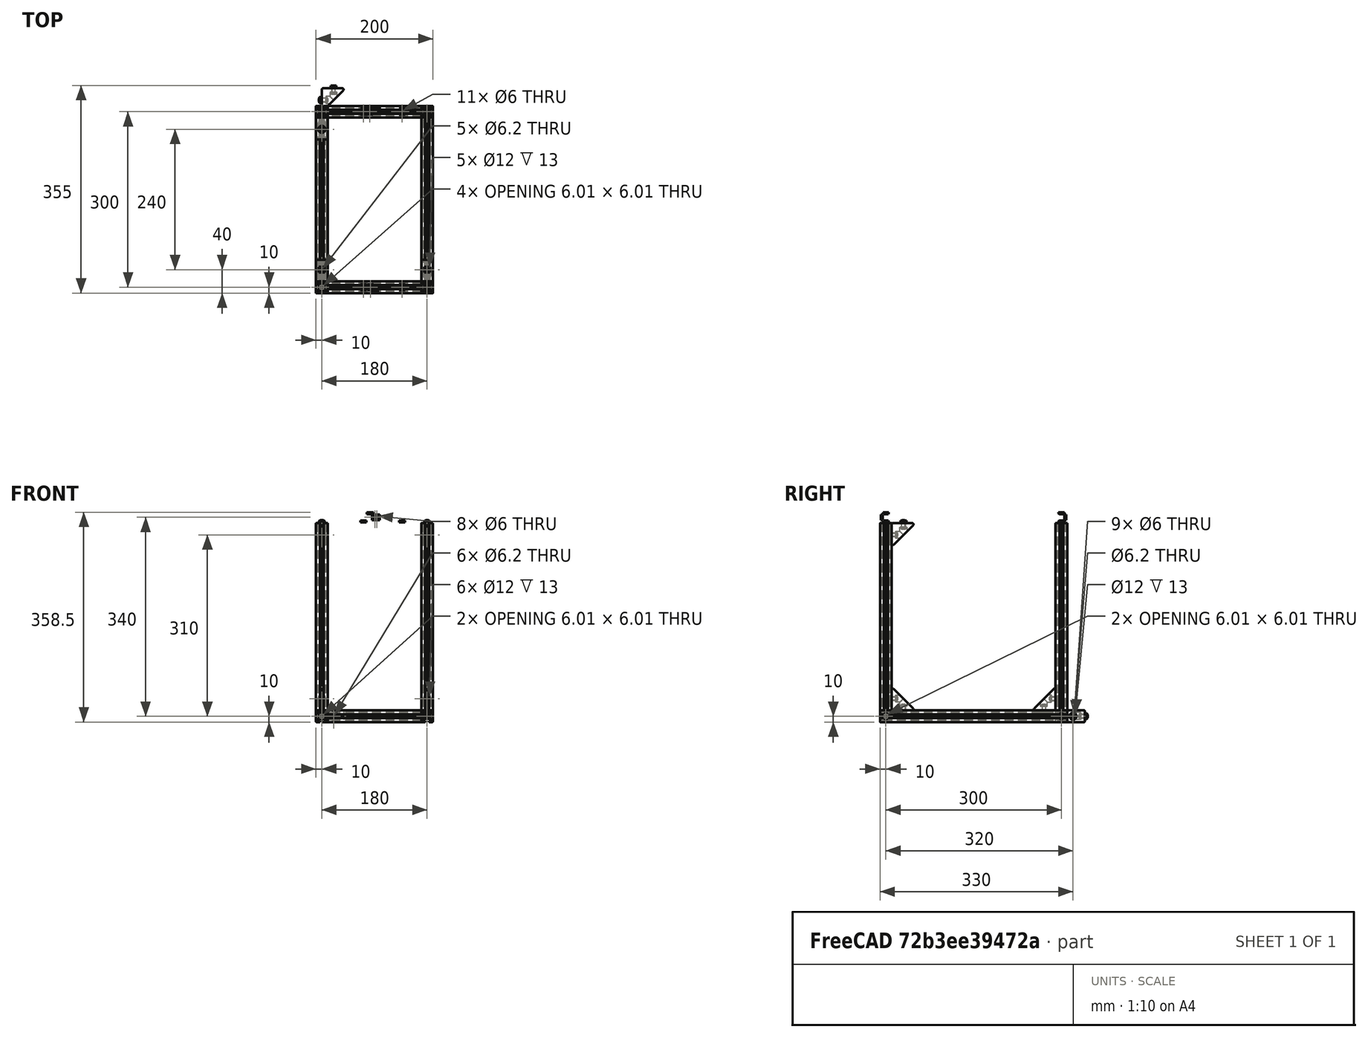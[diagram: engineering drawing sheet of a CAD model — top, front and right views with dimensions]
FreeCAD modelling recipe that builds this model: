
FCSTD DOCUMENT  (FreeCAD 0.17R9796 (Git))
Label: upright1
License: All rights reserved
LicenseURL: http://en.wikipedia.org/wiki/All_rights_reserved
objects: Part::Feature×57, Part::FeaturePython×16, App::Part×6, Part::Compound×5
note: 78 computed .brp shape members not serialized (recipe doc carries the construction recipe); baked Part::Feature solids carry a one-line shape summary decoded from their .brp

FEATURE [Part::Feature] Pocket003001  label="tslot32con"
  Placement = pos=(0,10,10) rot=(1,0,0;1.5708rad)
  shape: bbox 20 x 320 x 20 mm, 150 faces (baked)
FEATURE [Part::Feature] Pocket003002  label="tslot16"
  Placement = pos=(10,0,10) rot=(0,1,0;1.5708rad)
  shape: bbox 160 x 20 x 20 mm, 94 faces (baked)
FEATURE [Part::Feature] Pocket003006  label="tslot16_001"
  Placement = pos=(10,-300,10) rot=(0,1,0;1.5708rad)
  shape: bbox 160 x 20 x 20 mm, 94 faces (baked)
FEATURE [Part::Feature] Pocket003007  label="tslot32con_001"
  Placement = pos=(180,-310,10) rot=(0,0.707107,0.707107;3.14159rad)
  shape: bbox 20 x 320 x 20 mm, 150 faces (baked)
FEATURE [Part::FeaturePython] Screw  label="M6x25-Screw"  # Fasteners workbench fastener (typed FeaturePython)
  Placement = pos=(-4,0,10) rot=(0,-1,0;1.5708rad)
  diameter = 7
  invert = false
  length = 6
  matchOuter = false
  offset = 0
  thread = false
  type = 15
FEATURE [Part::FeaturePython] Screw001  label="M6x25-Screw004"  # Fasteners workbench fastener (typed FeaturePython)
  Placement = pos=(-4,-300,10) rot=(0,-1,0;1.5708rad)
  diameter = 7
  invert = false
  length = 6
  matchOuter = false
  offset = 0
  thread = false
  type = 15
FEATURE [Part::FeaturePython] Screw002  label="M6x25-Screw005"  # Fasteners workbench fastener (typed FeaturePython)
  Placement = pos=(184,0,10) rot=(0,1,0;1.5708rad)
  diameter = 7
  invert = false
  length = 6
  matchOuter = false
  offset = 0
  thread = false
  type = 15
FEATURE [Part::FeaturePython] Screw004  label="M6x25-Screw006"  # Fasteners workbench fastener (typed FeaturePython)
  Placement = pos=(184,-300,10) rot=(0,1,0;1.5708rad)
  diameter = 7
  invert = false
  length = 6
  matchOuter = false
  offset = 0
  thread = false
  type = 15
FEATURE [App::Part] Part  label="lower_frame"
  Group = -> [Pocket003001,Pocket003002,Pocket003006,Pocket003007,Screw,Screw001,Screw002,Screw004]
  License = CC BY 3.0
  LicenseURL = http://creativecommons.org/licenses/by/3.0/
  Origin = -> PartOrigin
FEATURE [Part::Feature] Pocket003008  label="tslot32con001"
  Placement = pos=(0,10,10) rot=(1,0,0;1.5708rad)
  shape: bbox 20 x 320 x 20 mm, 150 faces (baked)
FEATURE [Part::Feature] Pocket003009  label="tslot041"
  Placement = pos=(10,0,10) rot=(0,1,0;1.5708rad)
  shape: bbox 160 x 20 x 20 mm, 94 faces (baked)
FEATURE [Part::Feature] Pocket003010  label="tslot16_002"
  Placement = pos=(10,-300,10) rot=(0,1,0;1.5708rad)
  shape: bbox 160 x 20 x 20 mm, 94 faces (baked)
FEATURE [Part::Feature] Pocket003011  label="tslot32con_002"
  Placement = pos=(180,-310,10) rot=(0,0.707107,0.707107;3.14159rad)
  shape: bbox 20 x 320 x 20 mm, 150 faces (baked)
FEATURE [Part::FeaturePython] Screw005  label="M6x25-Screw007"  # Fasteners workbench fastener (typed FeaturePython)
  Placement = pos=(-4,0,10) rot=(0,-1,0;1.5708rad)
  diameter = 7
  invert = false
  length = 6
  matchOuter = false
  offset = 0
  thread = false
  type = 15
FEATURE [Part::FeaturePython] Screw006  label="M6x25-Screw008"  # Fasteners workbench fastener (typed FeaturePython)
  Placement = pos=(-4,-300,10) rot=(0,-1,0;1.5708rad)
  diameter = 7
  invert = false
  length = 6
  matchOuter = false
  offset = 0
  thread = false
  type = 15
FEATURE [Part::FeaturePython] Screw007  label="M6x25-Screw011"  # Fasteners workbench fastener (typed FeaturePython)
  Placement = pos=(184,0,10) rot=(0,1,0;1.5708rad)
  diameter = 7
  invert = false
  length = 6
  matchOuter = false
  offset = 0
  thread = false
  type = 15
FEATURE [Part::FeaturePython] Screw008  label="M6x25-Screw010"  # Fasteners workbench fastener (typed FeaturePython)
  Placement = pos=(184,-300,10) rot=(0,1,0;1.5708rad)
  diameter = 7
  invert = false
  length = 6
  matchOuter = false
  offset = 0
  thread = false
  type = 15
FEATURE [App::Part] Part001  label="upper_frame"
  Group = -> [Pocket003008,Pocket003009,Pocket003010,Pocket003011,Screw005,Screw006,Screw007,Screw008]
  License = CC BY 3.0
  LicenseURL = http://creativecommons.org/licenses/by/3.0/
  Origin = -> PartOrigin001
  Placement = pos=(0,0,340) rot=(0,0,1;0rad)
FEATURE [Part::Feature] Fillet004001  label="Fillet005"
  shape: bbox 37.5 x 37.5 x 20 mm, 26 faces (baked)
FEATURE [Part::FeaturePython] Screw009  label="M6x12-Screw"  # Fasteners workbench fastener (typed FeaturePython)
  Placement = pos=(7,20,10) rot=(0,1,0;1.5708rad)
  diameter = 4
  invert = false
  length = 1
  matchOuter = false
  offset = 0
  thread = false
  type = 20
FEATURE [Part::Feature] Body001  label="m6nutplate"
  Placement = pos=(-1.5,15,5) rot=(0,-1,0;1.5708rad)
  shape: bbox 3 x 10 x 10 mm, 9 faces (baked)
FEATURE [App::Part] Part002  label="cornerstonescrewnut"
  License = CC BY 3.0
  LicenseURL = http://creativecommons.org/licenses/by/3.0/
  Origin = -> PartOrigin002
  Placement = pos=(10,-50,20) rot=(0,-1,0;1.5708rad)
FEATURE [Part::FeaturePython] Screw010  label="M6x12-Screw001"  # Fasteners workbench fastener (typed FeaturePython)
  Placement = pos=(20,33,10) rot=(1,0,0;1.5708rad)
  diameter = 4
  invert = false
  length = 1
  matchOuter = false
  offset = 0
  thread = false
  type = 20
FEATURE [Part::Feature] Body002  label="m6nutplate001"
  Placement = pos=(15,41.5,5) rot=(0.57735,0.57735,0.57735;4.18879rad)
  shape: bbox 10 x 3 x 10 mm, 9 faces (baked)
FEATURE [Part::Feature] Fillet004002  label="Fillet006"
  shape: bbox 37.5 x 37.5 x 20 mm, 26 faces (baked)
FEATURE [Part::FeaturePython] Screw011  label="M6x12-Screw002"  # Fasteners workbench fastener (typed FeaturePython)
  Placement = pos=(7,20,10) rot=(0,1,0;1.5708rad)
  diameter = 4
  invert = false
  length = 1
  matchOuter = false
  offset = 0
  thread = false
  type = 20
FEATURE [Part::Feature] Body003  label="m6nutplate002"
  Placement = pos=(-1.5,15,5) rot=(0,-1,0;1.5708rad)
  shape: bbox 3 x 10 x 10 mm, 9 faces (baked)
FEATURE [Part::FeaturePython] Screw012  label="M6x12-Screw003"  # Fasteners workbench fastener (typed FeaturePython)
  Placement = pos=(20,33,10) rot=(1,0,0;1.5708rad)
  diameter = 4
  invert = false
  length = 1
  matchOuter = false
  offset = 0
  thread = false
  type = 20
FEATURE [Part::Feature] Body004  label="m6nutplate003"
  Placement = pos=(15,41.5,5) rot=(0.57735,0.57735,0.57735;4.18879rad)
  shape: bbox 10 x 3 x 10 mm, 9 faces (baked)
FEATURE [App::Part] Part003  label="cornerstonescrewnut001"
  Group = -> [Body003,Screw011,Fillet004002,Screw012,Body004,PartOrigin002,Body001,Screw009,Fillet004001,Screw010,Body002,Part002]
  License = CC BY 3.0
  LicenseURL = http://creativecommons.org/licenses/by/3.0/
  Origin = -> PartOrigin003
  Placement = pos=(190,-50,20) rot=(0,-1,0;1.5708rad)
FEATURE [Part::Feature] Fillet004003  label="Fillet007"
  shape: bbox 37.5 x 37.5 x 20 mm, 26 faces (baked)
FEATURE [Part::FeaturePython] Screw013  label="M6x12-Screw004"  # Fasteners workbench fastener (typed FeaturePython)
  Placement = pos=(7,20,10) rot=(0,1,0;1.5708rad)
  diameter = 4
  invert = false
  length = 1
  matchOuter = false
  offset = 0
  thread = false
  type = 20
FEATURE [Part::Feature] Body005  label="m6nutplate004"
  Placement = pos=(-1.5,15,5) rot=(0,-1,0;1.5708rad)
  shape: bbox 3 x 10 x 10 mm, 9 faces (baked)
FEATURE [Part::FeaturePython] Screw014  label="M6x12-Screw005"  # Fasteners workbench fastener (typed FeaturePython)
  Placement = pos=(20,33,10) rot=(1,0,0;1.5708rad)
  diameter = 4
  invert = false
  length = 1
  matchOuter = false
  offset = 0
  thread = false
  type = 20
FEATURE [Part::Feature] Body006  label="m6nutplate005"
  Placement = pos=(15,41.5,5) rot=(0.57735,0.57735,0.57735;4.18879rad)
  shape: bbox 10 x 3 x 10 mm, 9 faces (baked)
FEATURE [App::Part] Part004  label="cornerstonescrewnut002"
  Group = -> [Body005,Screw013,Fillet004003,Screw014,Body006]
  License = CC BY 3.0
  LicenseURL = http://creativecommons.org/licenses/by/3.0/
  Origin = -> PartOrigin004
  Placement = pos=(-10,-50,340) rot=(0,1,0;1.5708rad)
FEATURE [Part::Feature] Fillet004004  label="Fillet008"
  shape: bbox 37.5 x 37.5 x 20 mm, 26 faces (baked)
FEATURE [Part::FeaturePython] Screw015  label="M6x12-Screw006"  # Fasteners workbench fastener (typed FeaturePython)
  Placement = pos=(7,20,10) rot=(0,1,0;1.5708rad)
  diameter = 4
  invert = false
  length = 1
  matchOuter = false
  offset = 0
  thread = false
  type = 20
FEATURE [Part::Feature] Body007  label="m6nutplate006"
  Placement = pos=(-1.5,15,5) rot=(0,-1,0;1.5708rad)
  shape: bbox 3 x 10 x 10 mm, 9 faces (baked)
FEATURE [Part::FeaturePython] Screw016  label="M6x12-Screw007"  # Fasteners workbench fastener (typed FeaturePython)
  Placement = pos=(20,33,10) rot=(1,0,0;1.5708rad)
  diameter = 4
  invert = false
  length = 1
  matchOuter = false
  offset = 0
  thread = false
  type = 20
FEATURE [Part::Feature] Body008  label="m6nutplate007"
  Placement = pos=(15,41.5,5) rot=(0.57735,0.57735,0.57735;4.18879rad)
  shape: bbox 10 x 3 x 10 mm, 9 faces (baked)
FEATURE [App::Part] Part005  label="cornerstonescrewnut003"
  Group = -> [Body007,Screw015,Fillet004004,Screw016,Body008]
  License = CC BY 3.0
  LicenseURL = http://creativecommons.org/licenses/by/3.0/
  Origin = -> PartOrigin005
  Placement = pos=(170,-50,340) rot=(0,1,0;1.5708rad)
FEATURE [Part::Feature] Body009001  label="m6nutplate010"
  Placement = pos=(-1.5,15,5) rot=(0,-1,0;1.5708rad)
  shape: bbox 3 x 10 x 10 mm, 9 faces (baked)
FEATURE [Part::Feature] Body010001  label="m6nutplate011"
  Placement = pos=(15,41.5,5) rot=(0.57735,0.57735,0.57735;4.18879rad)
  shape: bbox 10 x 3 x 10 mm, 9 faces (baked)
FEATURE [Part::Feature] Screw018001  label="M6x12-Screw010"
  Placement = pos=(20,33,10) rot=(1,0,0;1.5708rad)
  shape: bbox 10.5 x 15.3 x 10.5 mm, 15 faces (baked)
FEATURE [Part::Feature] Screw017001  label="M6x12-Screw011"
  Placement = pos=(7,20,10) rot=(0,1,0;1.5708rad)
  shape: bbox 15.3 x 10.5 x 10.5 mm, 15 faces (baked)
FEATURE [Part::Feature] Fillet004005001  label="Fillet010"
  shape: bbox 37.5 x 37.5 x 20 mm, 26 faces (baked)
FEATURE [Part::Compound] Compound
  Links = -> [Body009001,Fillet004005001,Screw017001,Body010001,Screw018001]
  Placement = pos=(10,-250,340) rot=(0.707107,0,-0.707107;3.14159rad)
FEATURE [Part::Feature] Body010002  label="m6nutplate012"
  Placement = pos=(-1.5,15,5) rot=(0,-1,0;1.5708rad)
  shape: bbox 3 x 10 x 10 mm, 9 faces (baked)
FEATURE [Part::Feature] Body010003  label="m6nutplate013"
  Placement = pos=(15,41.5,5) rot=(0.57735,0.57735,0.57735;4.18879rad)
  shape: bbox 10 x 3 x 10 mm, 9 faces (baked)
FEATURE [Part::Feature] Screw018002  label="M6x12-Screw012"
  Placement = pos=(20,33,10) rot=(1,0,0;1.5708rad)
  shape: bbox 10.5 x 15.3 x 10.5 mm, 15 faces (baked)
FEATURE [Part::Feature] Screw018003  label="M6x12-Screw013"
  Placement = pos=(7,20,10) rot=(0,1,0;1.5708rad)
  shape: bbox 15.3 x 10.5 x 10.5 mm, 15 faces (baked)
FEATURE [Part::Feature] Fillet004005002  label="Fillet011"
  shape: bbox 37.5 x 37.5 x 20 mm, 26 faces (baked)
FEATURE [Part::Compound] Compound001
  Links = -> [Body010002,Fillet004005002,Screw018003,Body010003,Screw018002]
  Placement = pos=(190,-250,340) rot=(0.707107,0,-0.707107;3.14159rad)
FEATURE [Part::Feature] Body010004  label="m6nutplate014"
  Placement = pos=(-1.5,15,5) rot=(0,-1,0;1.5708rad)
  shape: bbox 3 x 10 x 10 mm, 9 faces (baked)
FEATURE [Part::Feature] Body010005  label="m6nutplate015"
  Placement = pos=(15,41.5,5) rot=(0.57735,0.57735,0.57735;4.18879rad)
  shape: bbox 10 x 3 x 10 mm, 9 faces (baked)
FEATURE [Part::Feature] Screw018004  label="M6x12-Screw014"
  Placement = pos=(20,33,10) rot=(1,0,0;1.5708rad)
  shape: bbox 10.5 x 15.3 x 10.5 mm, 15 faces (baked)
FEATURE [Part::Feature] Screw018005  label="M6x12-Screw015"
  Placement = pos=(7,20,10) rot=(0,1,0;1.5708rad)
  shape: bbox 15.3 x 10.5 x 10.5 mm, 15 faces (baked)
FEATURE [Part::Feature] Fillet004005003  label="Fillet012"
  shape: bbox 37.5 x 37.5 x 20 mm, 26 faces (baked)
FEATURE [Part::Compound] Compound002
  Links = -> [Body010004,Fillet004005003,Screw018005,Body010005,Screw018004]
  Placement = pos=(10,-290,60) rot=(0.57735,0.57735,-0.57735;4.18879rad)
FEATURE [Part::Feature] Body010006  label="m6nutplate016"
  Placement = pos=(-1.5,15,5) rot=(0,-1,0;1.5708rad)
  shape: bbox 3 x 10 x 10 mm, 9 faces (baked)
FEATURE [Part::Feature] Body010007  label="m6nutplate017"
  Placement = pos=(15,41.5,5) rot=(0.57735,0.57735,0.57735;4.18879rad)
  shape: bbox 10 x 3 x 10 mm, 9 faces (baked)
FEATURE [Part::Feature] Screw018006  label="M6x12-Screw016"
  Placement = pos=(20,33,10) rot=(1,0,0;1.5708rad)
  shape: bbox 10.5 x 15.3 x 10.5 mm, 15 faces (baked)
FEATURE [Part::Feature] Screw018007  label="M6x12-Screw017"
  Placement = pos=(7,20,10) rot=(0,1,0;1.5708rad)
  shape: bbox 15.3 x 10.5 x 10.5 mm, 15 faces (baked)
FEATURE [Part::Feature] Fillet004005004  label="Fillet013"
  shape: bbox 37.5 x 37.5 x 20 mm, 26 faces (baked)
FEATURE [Part::Compound] Compound003
  Links = -> [Body010006,Fillet004005004,Screw018007,Body010007,Screw018006]
  Placement = pos=(190,-290,60) rot=(0.57735,0.57735,-0.57735;4.18879rad)
FEATURE [Part::Feature] Pocket001001  label="tslot32"
  Placement = pos=(0,0,20) rot=(0,0,1;0rad)
  shape: bbox 20 x 20 x 320 mm, 94 faces (baked)
FEATURE [Part::Feature] Body010008  label="m6nutplate018"
  Placement = pos=(-1.5,15,5) rot=(0,-1,0;1.5708rad)
  shape: bbox 3 x 10 x 10 mm, 9 faces (baked)
FEATURE [Part::Feature] Body010009  label="m6nutplate019"
  Placement = pos=(15,41.5,5) rot=(0.57735,0.57735,0.57735;4.18879rad)
  shape: bbox 10 x 3 x 10 mm, 9 faces (baked)
FEATURE [Part::Feature] Screw018008  label="M6x12-Screw018"
  Placement = pos=(20,33,10) rot=(1,0,0;1.5708rad)
  shape: bbox 10.5 x 15.3 x 10.5 mm, 15 faces (baked)
FEATURE [Part::Feature] Screw018009  label="M6x12-Screw019"
  Placement = pos=(7,20,10) rot=(0,1,0;1.5708rad)
  shape: bbox 15.3 x 10.5 x 10.5 mm, 15 faces (baked)
FEATURE [Part::Feature] Fillet004005005  label="Fillet014"
  shape: bbox 37.5 x 37.5 x 20 mm, 26 faces (baked)
FEATURE [Part::Compound] Compound004
  Links = -> [Body010008,Fillet004005005,Screw018009,Body010009,Screw018008]
  Placement = pos=(-10,-10,60) rot=(0.57735,-0.57735,0.57735;4.18879rad)
FEATURE [Part::Feature] Pocket003012  label="tslot32_001"
  Placement = pos=(0,-300,20) rot=(0,0,1;0rad)
  shape: bbox 20 x 20 x 320 mm, 94 faces (baked)
FEATURE [Part::Feature] Pocket003013  label="tslot32_002"
  Placement = pos=(180,0,20) rot=(0,0,1;0rad)
  shape: bbox 20 x 20 x 320 mm, 94 faces (baked)
FEATURE [Part::Feature] Pocket003014  label="tslot32_003"
  Placement = pos=(180,-300,20) rot=(0,0,1;0rad)
  shape: bbox 20 x 20 x 320 mm, 94 faces (baked)
FEATURE [Part::Feature] Chamfer001001  label="m6nutplate020"
  Placement = pos=(88,-295,358.5) rot=(-0.707107,0.707107,0;3.14159rad)
  shape: bbox 10 x 10 x 3 mm, 9 faces (baked)
FEATURE [Part::Feature] Chamfer001002  label="m6nutplate021"
  Placement = pos=(96,-308.5,355) rot=(0.57735,-0.57735,-0.57735;4.18879rad)
  shape: bbox 10 x 3 x 10 mm, 9 faces (baked)
FEATURE [Part::Feature] Chamfer001003  label="m6nutplate022"
  Placement = pos=(87,5,358.5) rot=(0.707107,-0.707107,0;3.14159rad)
  shape: bbox 10 x 10 x 3 mm, 9 faces (baked)
FEATURE [Part::Feature] Chamfer001004  label="m6nutplate023"
  Placement = pos=(99,8.4,345) rot=(0.57735,-0.57735,0.57735;2.0944rad)
  shape: bbox 10 x 3 x 10 mm, 9 faces (baked)
FEATURE [Part::Feature] Chamfer001005  label="m6nutplate024"
  Placement = pos=(76,-305,341.6) rot=(0,0,1;1.5708rad)
  shape: bbox 10 x 10 x 3 mm, 9 faces (baked)
FEATURE [Part::Feature] Chamfer001006  label="m6nutplate025"
  Placement = pos=(142,-305,341.6) rot=(0,0,1;1.5708rad)
  shape: bbox 10 x 10 x 3 mm, 9 faces (baked)
FEATURE [Part::Feature] Chamfer001007  label="m6nutplate026"
  Placement = pos=(142,-5,341.6) rot=(0,0,1;1.5708rad)
  shape: bbox 10 x 10 x 3 mm, 9 faces (baked)
FEATURE [Part::Feature] Chamfer001008  label="m6nutplate027"
  Placement = pos=(76,-5,341.6) rot=(0,0,1;1.5708rad)
  shape: bbox 10 x 10 x 3 mm, 9 faces (baked)
